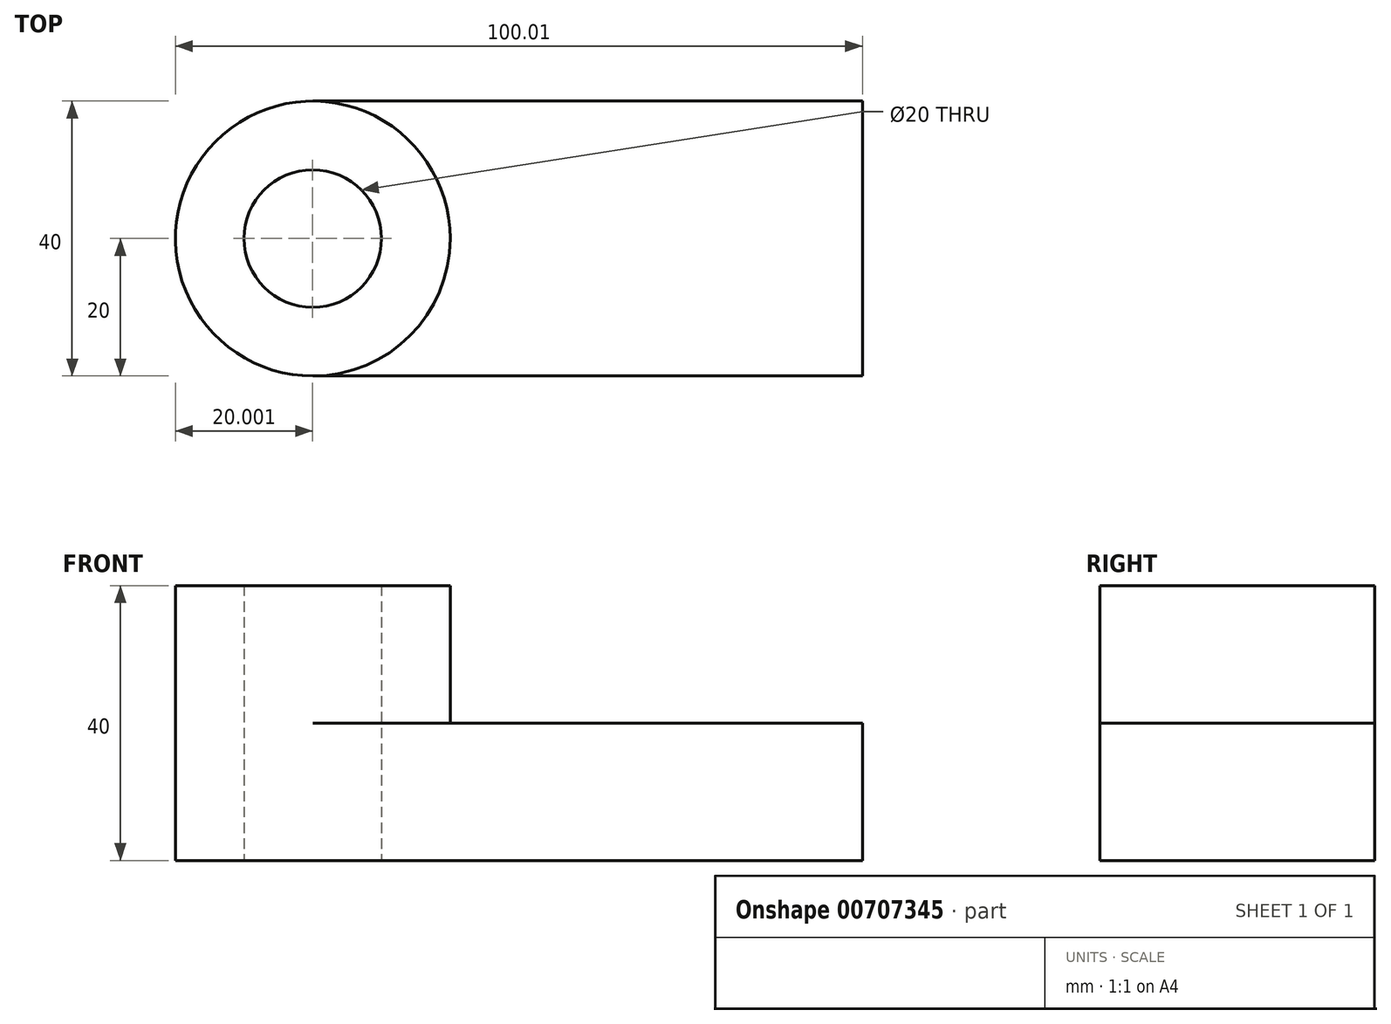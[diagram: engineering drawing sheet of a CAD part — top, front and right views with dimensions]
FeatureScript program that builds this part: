
annotation { "Feature Type Name" : "Feature", "Feature Type Description" : "" }
export const myFeature = defineFeature(function(context is Context, id is Id, definition is map)
    precondition{}
    {
        {
            var Q0;
            Q0=qCreatedBy(makeId("Top.planeOp"),FACE);
            var sketch = newSketch(context, id + "F0", { "sketchPlane" : qUnion([Q0])});
            skCircle(sketch, "E0", {"center": v(-108.64, 0) * mm, "radius": 20 * mm});
            skLineSegment(sketch, "E1.bottom", {"start": v(-108.63, 20) * mm, "end": v(-28.63, 20) * mm});
            skLineSegment(sketch, "E1.top", {"start": v(-108.63, -20) * mm, "end": v(-28.63, -20) * mm});
            skLineSegment(sketch, "E1.right", {"start": v(-28.63, 20) * mm, "end": v(-28.63, -20) * mm});
            skCircle(sketch, "E2", {"center": v(-108.64, 0) * mm, "radius": 10 * mm});
            skSolve(sketch);
        }
        {
            var Q0;
            Q0=makeQuery(id+"F0.imprint","IMPRINT",FACE,{"disambiguationData":[TD([[makeQuery(id+"F0.imprint","IMPRINT",EDGE,{"derivedFrom":sQuery(id+"F0.wireOp",EDGE,"E2")}),-1.0]])]});
            extrude(context, id + "F1", {"entities" : qUnion([Q0]), "depth" : 40 * mm, "offsetDistance" : 25 * mm});
        }
        {
            var Q0;
            {var subQ0=sQuery(id+"F0.wireOp",EDGE,"E1.bottom");Q0=makeQuery(id+"F0.imprint","IMPRINT",FACE,{"disambiguationData":[TD([[makeQuery(id+"F0.imprint","IMPRINT",EDGE,{"derivedFrom":subQ0}),-1.0]])]});}
            extrude(context, id + "F2", {"entities" : qUnion([Q0]), "operationType" : NewBodyOperationType.ADD, "depth" : 20 * mm, "offsetDistance" : 25 * mm});
        }
    });
